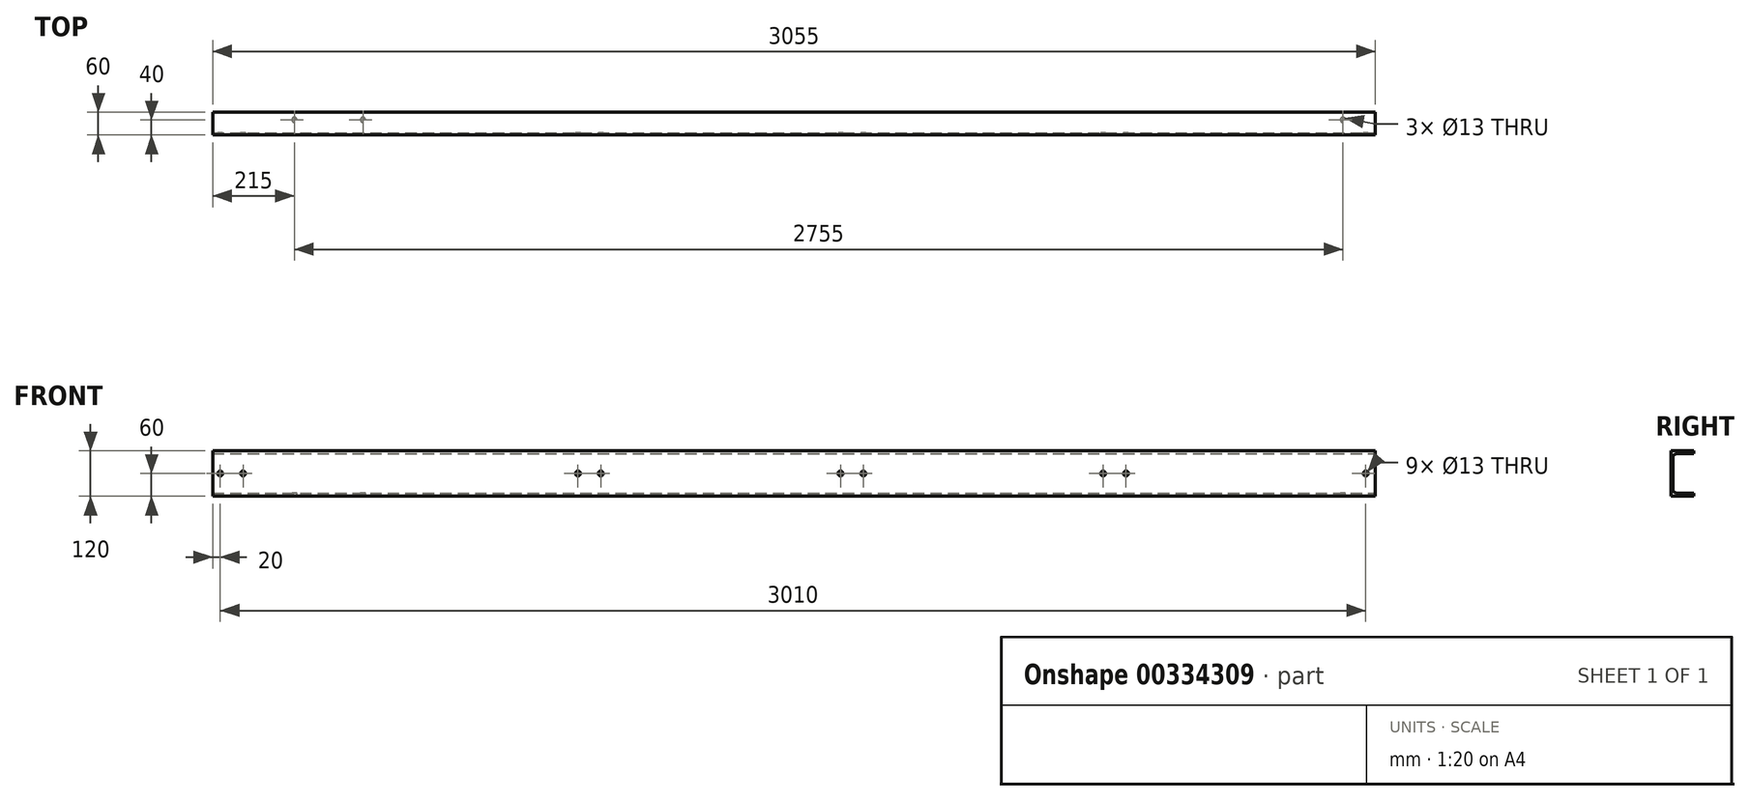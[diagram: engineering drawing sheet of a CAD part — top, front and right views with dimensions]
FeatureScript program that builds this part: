
annotation { "Feature Type Name" : "Feature", "Feature Type Description" : "" }
export const myFeature = defineFeature(function(context is Context, id is Id, definition is map)
    precondition{}
    {
        {
            assignVariable(context, id + "F0", {"name" : "L_Pro", "anyValue" : 2755 + 300});
        }
        {
            assignVariable(context, id + "F1", {"name" : "L_Hoe", "anyValue" : 120});
        }
        {
            var Q0;
            Q0=qCreatedBy(makeId("Right.planeOp"),FACE);
            var sketch = newSketch(context, id + "F2", { "sketchPlane" : qUnion([Q0])});
            skLineSegment(sketch, "E0", {"start": v(0, 0) * mm, "end": v(-60, 0) * mm});
            skLineSegment(sketch, "E1", {"start": v(-60, 0) * mm, "end": v(-60, 120) * mm});
            skLineSegment(sketch, "E2", {"start": v(-60, 120) * mm, "end": v(0, 120) * mm});
            skLineSegment(sketch, "E3", {"start": v(0, 120) * mm, "end": v(0, 112) * mm});
            skLineSegment(sketch, "E4", {"start": v(0, 112) * mm, "end": v(-43, 112) * mm});
            skLineSegment(sketch, "E5", {"start": v(-55, 100) * mm, "end": v(-55, 20) * mm});
            skLineSegment(sketch, "E6", {"start": v(-43, 8) * mm, "end": v(0, 8) * mm});
            skLineSegment(sketch, "E7", {"start": v(0, 8) * mm, "end": v(0, 0) * mm});
            skPoint(sketch, "E8.visualSharp", {"position": v(-55, 112) * mm});
            skArc(sketch, "E8.filletArc", {"start": v(-43, 112) * mm, "mid": v(-51.49, 108.49) * mm, "end": v(-55, 100) * mm});
            skPoint(sketch, "E9.visualSharp", {"position": v(-55, 8) * mm});
            skArc(sketch, "E9.filletArc", {"start": v(-55, 20) * mm, "mid": v(-51.49, 11.51) * mm, "end": v(-43, 8) * mm});
            skSolve(sketch);
        }
        {
            var Q0;
            Q0=qSketchRegion(id+"F2",true);
            var Q1;
            Q1=qConstructionFilter(qBodyType(qCreatedBy(id+"F2",EDGE),BodyType.WIRE),ConstructionObject.NO);
            extrude(context, id + "F3", {"entities" : qUnion([Q0]), "surfaceEntities" : qUnion([Q1]), "oppositeDirection" : true, "depth" : (getVariable(context, 'L_Pro')) * mm});
        }
        {
            var Q0;
            Q0=makeQuery(id+"F3.opExtrude","SWEPT_FACE",FACE,{"disambiguationData":[OSD([sQuery(id+"F2.wireOp",EDGE,"E6")])]});
            var sketch = newSketch(context, id + "F4", { "sketchPlane" : qUnion([Q0])});
            skCircle(sketch, "E10", {"center": v(-85, -20) * mm, "radius": 6.5 * mm});
            skCircle(sketch, "E11", {"center": v(-265, -20) * mm, "radius": 6.5 * mm, "construction": true});
            skCircle(sketch, "E12", {"center": v(-2840, -20) * mm, "radius": 6.5 * mm});
            skCircle(sketch, "E13", {"center": v(-2660, -20) * mm, "radius": 6.5 * mm});
            skSolve(sketch);
        }
        {
            var Q0;
            Q0=makeQuery(id+"F4.imprint","IMPRINT",FACE,{"disambiguationData":[TD([[makeQuery(id+"F4.imprint","IMPRINT",EDGE,{"derivedFrom":sQuery(id+"F4.wireOp",EDGE,"E12")}),1.0]])]});
            var Q1;
            Q1=makeQuery(id+"F4.imprint","IMPRINT",FACE,{"disambiguationData":[TD([[makeQuery(id+"F4.imprint","IMPRINT",EDGE,{"derivedFrom":sQuery(id+"F4.wireOp",EDGE,"E13")}),1.0]])]});
            var Q2;
            Q2=makeQuery(id+"F4.imprint","IMPRINT",FACE,{"disambiguationData":[TD([[makeQuery(id+"F4.imprint","IMPRINT",EDGE,{"derivedFrom":sQuery(id+"F4.wireOp",EDGE,"E10")}),1.0]])]});
            extrude(context, id + "F5", {"entities" : qUnion([Q0, Q1, Q2]), "operationType" : NewBodyOperationType.REMOVE, "endBound" : BoundingType.UP_TO_NEXT, "oppositeDirection" : true, "depth" : (2 * getVariable(context, 'L_Hoe')) * mm});
        }
        {
            var Q0;
            Q0=makeQuery(id+"F3.opExtrude","SWEPT_FACE",FACE,{"disambiguationData":[OSD([sQuery(id+"F2.wireOp",EDGE,"E1")])]});
            var sketch = newSketch(context, id + "F6", { "sketchPlane" : qUnion([Q0])});
            skCircle(sketch, "E14", {"center": v(-3035, 60) * mm, "radius": 6.5 * mm});
            skPoint(sketch, "E14.centerSnap0", {"position": v(-3055, 60) * mm});
            skCircle(sketch, "E15", {"center": v(-2975, 60) * mm, "radius": 6.5 * mm});
            skCircle(sketch, "E16", {"center": v(-2095, 60) * mm, "radius": 6.5 * mm});
            skCircle(sketch, "E17", {"center": v(-2035, 60) * mm, "radius": 6.5 * mm});
            skCircle(sketch, "E18", {"center": v(-1405, 60) * mm, "radius": 6.5 * mm});
            skCircle(sketch, "E19", {"center": v(-1345, 60) * mm, "radius": 6.5 * mm});
            skCircle(sketch, "E20", {"center": v(-715, 60) * mm, "radius": 6.5 * mm});
            skCircle(sketch, "E21", {"center": v(-655, 60) * mm, "radius": 6.5 * mm});
            skCircle(sketch, "E22", {"center": v(-25, 60) * mm, "radius": 6.5 * mm});
            skSolve(sketch);
        }
        {
            var Q0;
            Q0=qSketchRegion(id+"F6",true);
            extrude(context, id + "F7", {"entities" : qUnion([Q0]), "operationType" : NewBodyOperationType.REMOVE, "endBound" : BoundingType.THROUGH_ALL, "oppositeDirection" : true, "depth" : 25 * mm});
        }
    });
